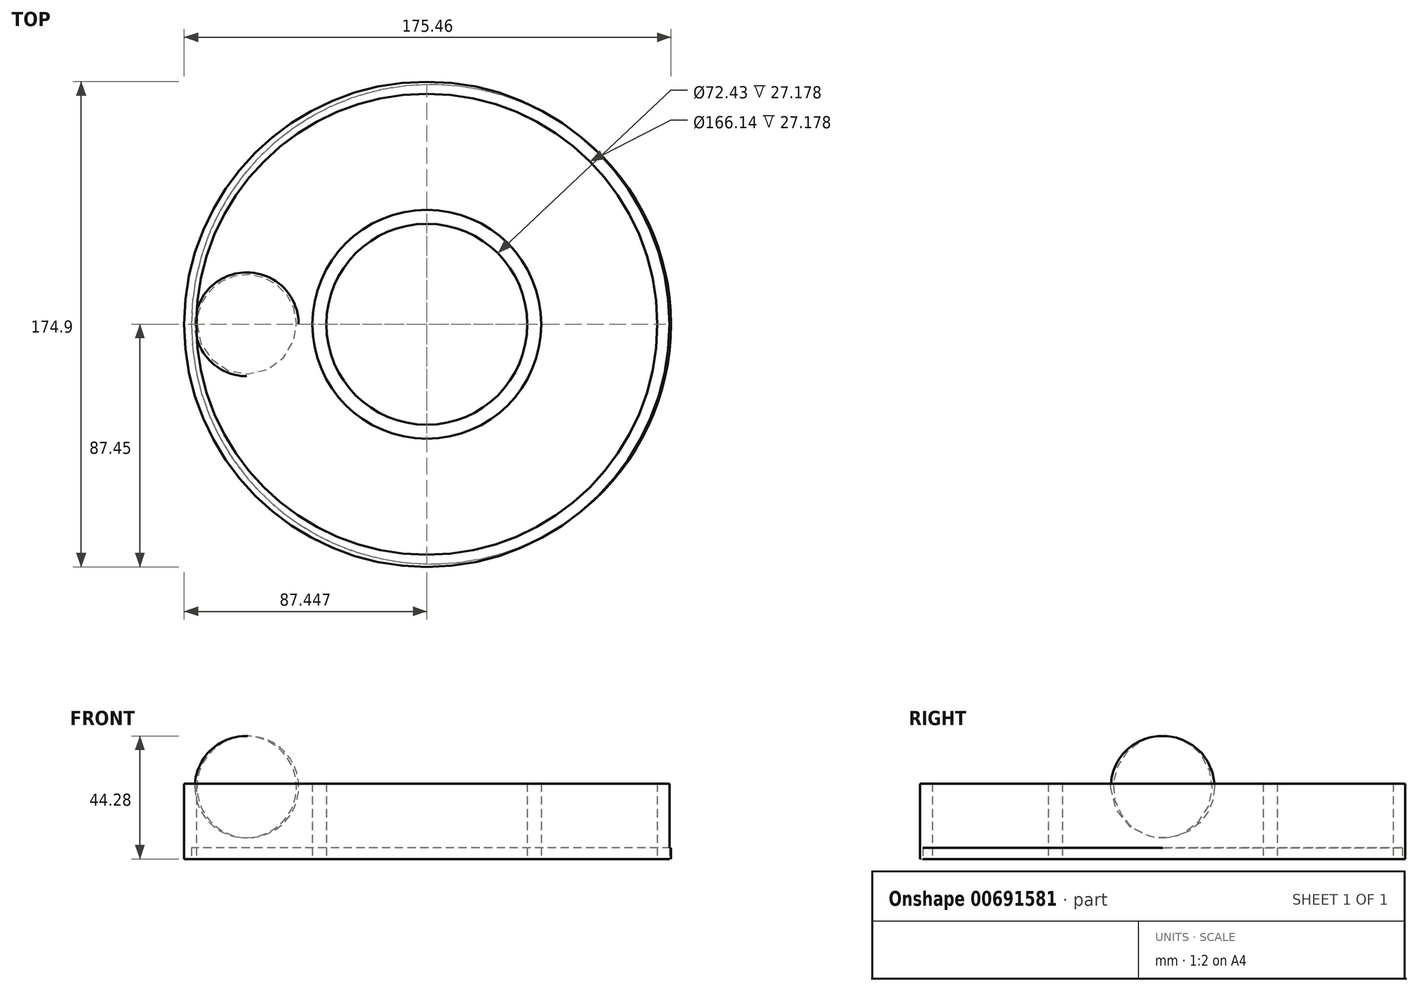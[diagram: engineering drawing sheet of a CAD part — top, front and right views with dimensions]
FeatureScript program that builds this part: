
annotation { "Feature Type Name" : "Feature", "Feature Type Description" : "" }
export const myFeature = defineFeature(function(context is Context, id is Id, definition is map)
    precondition{}
    {
        {
            var Q0;
            Q0=qCreatedBy(makeId("Top.planeOp"),FACE);
            var sketch = newSketch(context, id + "F0", { "sketchPlane" : qUnion([Q0])});
            skCircle(sketch, "E0", {"center": v(-61.87, 0) * mm, "radius": 87.45 * mm});
            skCircle(sketch, "E1", {"center": v(-61.87, 0) * mm, "radius": 83.07 * mm});
            skCircle(sketch, "E2", {"center": v(-61.87, 0) * mm, "radius": 41.26 * mm});
            skCircle(sketch, "E3", {"center": v(-61.87, 0) * mm, "radius": 36.21 * mm});
            skSolve(sketch);
        }
        {
            var Q0;
            Q0=makeQuery(id+"F0.imprint","IMPRINT",FACE,{"disambiguationData":[TD([[makeQuery(id+"F0.imprint","IMPRINT",EDGE,{"derivedFrom":sQuery(id+"F0.wireOp",EDGE,"E0")}),1.0]])]});
            var Q1;
            Q1=makeQuery(id+"F0.imprint","IMPRINT",FACE,{"disambiguationData":[TD([[makeQuery(id+"F0.imprint","IMPRINT",EDGE,{"derivedFrom":sQuery(id+"F0.wireOp",EDGE,"E2")}),1.0]])]});
            extrude(context, id + "F1", {"entities" : qUnion([Q0, Q1]), "depth" : 27.18 * mm, "offsetDistance" : 25.4 * mm});
        }
        {
            var Q0;
            Q0=qCreatedBy(makeId("Top.planeOp"),FACE);
            var sketch = newSketch(context, id + "F2", { "sketchPlane" : qUnion([Q0])});
            skCircle(sketch, "E4", {"center": v(-60.29, 0) * mm, "radius": 86.43 * mm});
            skSolve(sketch);
        }
        {
            var Q0;
            Q0 = qSketchRegion(id + "F2", true);
            extrude(context, id + "F3", {"entities" : qUnion([Q0]), "depth" : 4.06 * mm, "offsetDistance" : 25.4 * mm});
        }
        {
            var Q0;
            Q0=qCreatedBy(makeId("Front.planeOp"),FACE);
            var sketch = newSketch(context, id + "F4", { "sketchPlane" : qUnion([Q0])});
            skArc(sketch, "E5", {"start": v(-126.88, 44.27) * mm, "mid": v(-144.69, 25.86) * mm, "end": v(-126.66, 7.66) * mm});
            skLineSegment(sketch, "E6", {"start": v(-126.88, 44.27) * mm, "end": v(-126.66, 7.66) * mm});
            skLineSegment(sketch, "E7", {"start": v(-126.88, 70.17) * mm, "end": v(-126.88, -26.02) * mm, "construction": true});
            skSolve(sketch);
        }
        {
            var Q0;
            Q0 = qSketchRegion(id + "F4", true);
            var Q1;
            Q1=sQuery(id+"F4.wireOp",EDGE,"E6");
            revolve(context, id + "F5", {"entities" : qUnion([Q0]), "axis" : qUnion([Q1]), "revolveType" : RevolveType.FULL});
        }
    });
